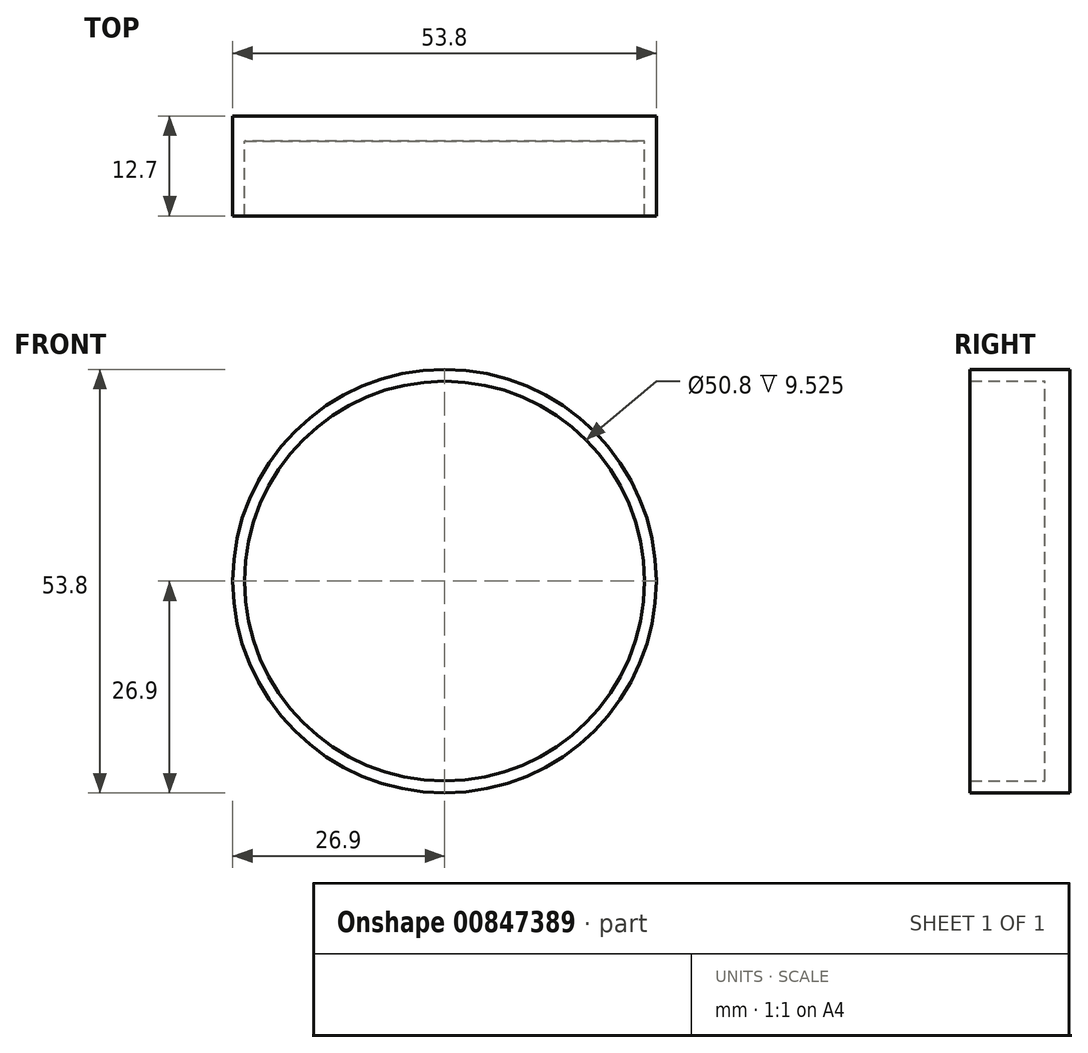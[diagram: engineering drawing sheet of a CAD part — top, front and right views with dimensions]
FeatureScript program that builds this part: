
annotation { "Feature Type Name" : "Feature", "Feature Type Description" : "" }
export const myFeature = defineFeature(function(context is Context, id is Id, definition is map)
    precondition{}
    {
        {
            var Q0;
            Q0=qCreatedBy(makeId("Front.planeOp"),FACE);
            var sketch = newSketch(context, id + "F0", { "sketchPlane" : qUnion([Q0])});
            skCircle(sketch, "E0", {"center": v(0, 0) * mm, "radius": 25.4 * mm});
            skCircle(sketch, "E1", {"center": v(0, 0) * mm, "radius": 26.9 * mm});
            skSolve(sketch);
        }
        {
            var Q0;
            Q0=makeQuery(id+"F0.imprint","IMPRINT",FACE,{"disambiguationData":[TD([[makeQuery(id+"F0.imprint","IMPRINT",EDGE,{"derivedFrom":sQuery(id+"F0.wireOp",EDGE,"E0")}),1.0]])]});
            var Q1;
            Q1=makeQuery(id+"F0.imprint","IMPRINT",FACE,{"disambiguationData":[TD([[makeQuery(id+"F0.imprint","IMPRINT",EDGE,{"derivedFrom":sQuery(id+"F0.wireOp",EDGE,"E0")}),-1.0]])]});
            extrude(context, id + "F1", {"entities" : qUnion([Q0, Q1]), "depth" : 3.17 * mm, "offsetDistance" : 25 * mm});
        }
        {
            var Q0;
            Q0 = qSketchRegion(id + "F0", true);
            extrude(context, id + "F2", {"entities" : qUnion([Q0]), "operationType" : NewBodyOperationType.ADD, "depth" : 12.7 * mm, "offsetDistance" : 25 * mm});
        }
    });
